# Revit family: NLRS_33_RB_DO_BILCO_dakluik_D-50T
name_source: partatom
category: Doors
revit_build: Autodesk Revit 2015 (Build: 20140223_1515(x64)
units: mm (PartAtom-declared; Revit-internal decimal feet)

## types (1)
- RoofAccessHatchTypeD-50T
    Description = Aluminium access hatch
    Height = 405 mm
    RWA = Yes
    Rough Height = 0 mm  [stored 0 ft]
    Rough Width = 0 mm  [stored 0 ft]
    Thickness = 0 mm  [stored 0 ft]
    aansluiting BMC = Yes
    antislip profilering = Yes
    belasting = 0.00 kg/m²
    betegelbaar = Yes
    brandwerend 120 min = Yes
    brandwerend 30 min = Yes
    brandwerend 60 min = Yes
    brandwerend 90 min = Yes
    breedte = 2228 mm  [stored 7.30971 ft]
    breedte_paneel = 1091 mm
    breuklast kN = 0
    cilinderslot = Yes
    dagmaatbreedte = 2000 mm  [stored 6.56168 ft]
    dagmaatlengte = 1500 mm  [stored 4.92126 ft]
    doorlopende ladderboom = Yes
    geluidsreductie (dB) = 0
    gewicht = 0.00 kN
    hellingshoek = 5.00°
    hoogte = 405 mm
    hoogte_aandrijving = 325 mm  [stored 1.06627 ft]
    hoogte_opstand = 305 mm
    inhaakbeugel = Yes
    inhaakladder = Yes
    isolatie = Yes
    isolatiewaarde = 0.0000 (m²·K)/W
    lengte = 1728 mm
    lengte_paneel = 1598 mm  [stored 5.24278 ft]
    loopslot = Yes
    materiaal = bcb_aluminium
    materiaal_secundair = <By Category>
    muurbeuegels = Yes
    netto doorlaat = 0 m²
    omranding = Yes
    omranding hoekprofiel = Yes
    omranding waterafvoerend = Yes
    openingshoek = 0.00°
    openstand vergrendeling = Yes
    positie_paneel = 0 mm  [stored 0 ft]
    schaartrap = <None>
    scharnierend = Yes
    slotbeugel = 0 mm  [stored 0 ft]
    sluiting_inbus = 0
    thermische onderbreking = Yes
    tranenplaat = Yes
    uitloopleuning = Yes
    uitschuifbare leuning = 0 mm  [stored 0 ft]
    uitstapbordes = Yes
    vaste ladder = Yes
    vaste ladder met kooi = Yes
    veersysteem = Yes
    veiligheidsrailing = Yes
    vlak = Yes
    voetplaten = Yes
    waterdicht = Yes

note: [stored X ft] marks values corroborated as IEEE doubles in the binary element streams (Revit-internal decimal feet)

## geometry (parser evidence)
native form markers: Blend x786, Sweep x20
no freeform markers — native parametric forms only
